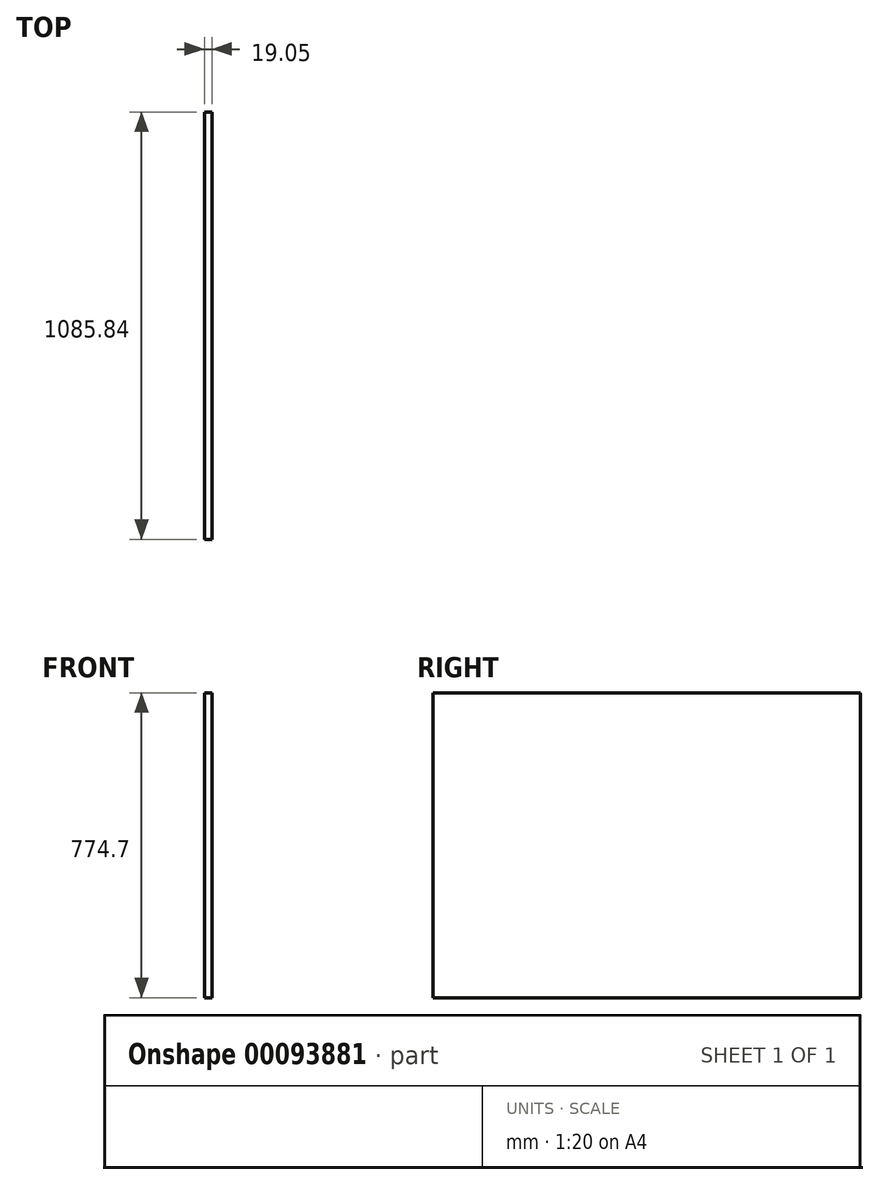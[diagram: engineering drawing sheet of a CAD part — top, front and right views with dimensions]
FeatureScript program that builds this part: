
annotation { "Feature Type Name" : "Feature", "Feature Type Description" : "" }
export const myFeature = defineFeature(function(context is Context, id is Id, definition is map)
    precondition{}
    {
        {
            var Q0;
            Q0=qCreatedBy(makeId("Right.planeOp"),FACE);
            var sketch = newSketch(context, id + "F0", { "sketchPlane" : qUnion([Q0])});
            skLineSegment(sketch, "E0.bottom", {"start": v(-542.93, 774.7) * mm, "end": v(542.93, 774.7) * mm});
            skLineSegment(sketch, "E0.top", {"start": v(-542.93, 0) * mm, "end": v(542.93, 0) * mm});
            skLineSegment(sketch, "E0.left", {"start": v(-542.93, 774.7) * mm, "end": v(-542.93, 0) * mm});
            skLineSegment(sketch, "E0.right", {"start": v(542.93, 774.7) * mm, "end": v(542.93, 0) * mm});
            skSolve(sketch);
        }
        {
            var Q0;
            Q0=qSketchRegion(id+"F0",true);
            extrude(context, id + "F1", {"entities" : qUnion([Q0]), "depth" : 19.05 * mm});
        }
    });
